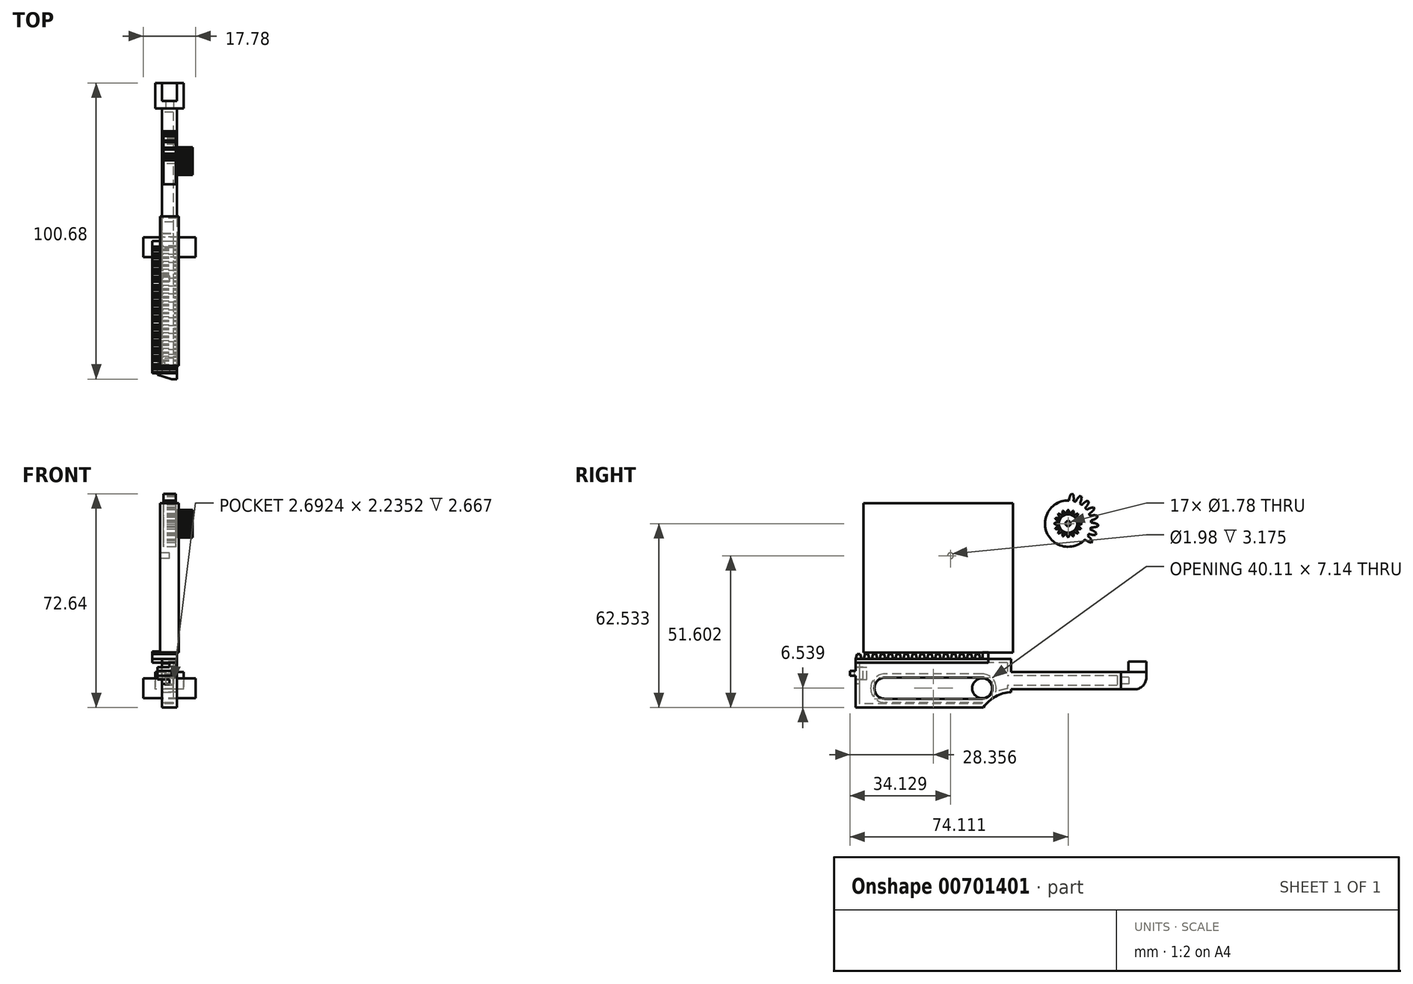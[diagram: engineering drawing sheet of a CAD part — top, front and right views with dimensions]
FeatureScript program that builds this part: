
annotation { "Feature Type Name" : "Feature", "Feature Type Description" : "" }
export const myFeature = defineFeature(function(context is Context, id is Id, definition is map)
    precondition{}
    {
        {
            var Q0;
            Q0=qCreatedBy(makeId("Right.planeOp"),FACE);
            var sketch = newSketch(context, id + "F0", { "sketchPlane" : qUnion([Q0])});
            skLineSegment(sketch, "E0.bottom", {"start": v(23, 9.46) * mm, "end": v(-29.8, 9.46) * mm});
            skLineSegment(sketch, "E0.top", {"start": v(23, -7) * mm, "end": v(-29.8, -7) * mm});
            skLineSegment(sketch, "E0.left", {"start": v(23, 9.46) * mm, "end": v(23, -7) * mm});
            skLineSegment(sketch, "E0.right", {"start": v(-29.8, 9.46) * mm, "end": v(-29.8, -7) * mm});
            skLineSegment(sketch, "E1.bottom", {"start": v(60.35, 5.06) * mm, "end": v(23, 5.06) * mm});
            skLineSegment(sketch, "E1.top", {"start": v(60.35, -0.83) * mm, "end": v(23, -0.83) * mm});
            skLineSegment(sketch, "E1.left", {"start": v(60.35, 5.06) * mm, "end": v(60.35, -0.83) * mm});
            skLineSegment(sketch, "E1.right", {"start": v(23, 5.06) * mm, "end": v(23, -0.83) * mm});
            skSolve(sketch);
        }
        {
            var Q0;
            Q0 = qSketchRegion(id + "F0", true);
            extrude(context, id + "F1", {"entities" : qUnion([Q0]), "endBound" : BoundingType.SYMMETRIC, "depth" : 5.08 * mm, "offsetDistance" : 25.4 * mm});
        }
        {
            var Q0;
            Q0=makeQuery(id+"F1.opExtrude","CAP_FACE",FACE,{"disambiguationData":[OSD([sQuery(id+"F0.wireOp",EDGE,"E0.bottom"),sQuery(id+"F0.wireOp",EDGE,"E0.top"),sQuery(id+"F0.wireOp",EDGE,"E0.left"),sQuery(id+"F0.wireOp",EDGE,"E0.right"),sQuery(id+"F0.wireOp",EDGE,"E1.bottom"),sQuery(id+"F0.wireOp",EDGE,"E1.top"),sQuery(id+"F0.wireOp",EDGE,"E1.left")])],"isStart":true});
            var sketch = newSketch(context, id + "F2", { "sketchPlane" : qUnion([Q0])});
            skLineSegment(sketch, "E2.bottom", {"start": v(-13.2, 3.1) * mm, "end": v(20, 3.1) * mm});
            skLineSegment(sketch, "E2.top", {"start": v(-13.2, -4.03) * mm, "end": v(20, -4.03) * mm});
            skLineSegment(sketch, "E2.left", {"start": v(-16.66, -0.35) * mm, "end": v(-16.66, -0.58) * mm});
            skLineSegment(sketch, "E2.right", {"start": v(23.45, -0.35) * mm, "end": v(23.45, -0.58) * mm});
            skPoint(sketch, "E3.visualSharp", {"position": v(23.45, 3.1) * mm});
            skArc(sketch, "E3.filletArc", {"start": v(23.45, -0.35) * mm, "mid": v(22.44, 2.1) * mm, "end": v(20, 3.1) * mm});
            skPoint(sketch, "E4.visualSharp", {"position": v(23.45, -4.03) * mm});
            skArc(sketch, "E4.filletArc", {"start": v(20, -4.03) * mm, "mid": v(22.44, -3.02) * mm, "end": v(23.45, -0.58) * mm});
            skPoint(sketch, "E5.visualSharp", {"position": v(-16.66, 3.1) * mm});
            skArc(sketch, "E5.filletArc", {"start": v(-13.2, 3.1) * mm, "mid": v(-15.65, 2.1) * mm, "end": v(-16.66, -0.35) * mm});
            skPoint(sketch, "E6.visualSharp", {"position": v(-16.66, -4.03) * mm});
            skArc(sketch, "E6.filletArc", {"start": v(-16.66, -0.58) * mm, "mid": v(-15.65, -3.02) * mm, "end": v(-13.2, -4.03) * mm});
            skSolve(sketch);
        }
        {
            var Q0;
            Q0 = qSketchRegion(id + "F2", true);
            var Q1;
            Q1=makeQuery(id+"F1.opExtrude","CAP_FACE",FACE,{"disambiguationData":[OSD([sQuery(id+"F0.wireOp",EDGE,"E0.bottom"),sQuery(id+"F0.wireOp",EDGE,"E0.top"),sQuery(id+"F0.wireOp",EDGE,"E0.left"),sQuery(id+"F0.wireOp",EDGE,"E0.right"),sQuery(id+"F0.wireOp",EDGE,"E1.bottom"),sQuery(id+"F0.wireOp",EDGE,"E1.top"),sQuery(id+"F0.wireOp",EDGE,"E1.left")])],"isStart":false});
            extrude(context, id + "F3", {"entities" : qUnion([Q0]), "operationType" : NewBodyOperationType.REMOVE, "endBound" : BoundingType.UP_TO_SURFACE, "oppositeDirection" : true, "depth" : 25.4 * mm, "endBoundEntityFace" : qUnion([Q1]), "offsetDistance" : 25.4 * mm});
        }
        {
            var Q0;
            Q0=makeQuery(id+"F1.opExtrude","CAP_FACE",FACE,{"disambiguationData":[OSD([sQuery(id+"F0.wireOp",EDGE,"E0.bottom"),sQuery(id+"F0.wireOp",EDGE,"E0.top"),sQuery(id+"F0.wireOp",EDGE,"E0.left"),sQuery(id+"F0.wireOp",EDGE,"E0.right"),sQuery(id+"F0.wireOp",EDGE,"E1.bottom"),sQuery(id+"F0.wireOp",EDGE,"E1.top"),sQuery(id+"F0.wireOp",EDGE,"E1.left")])],"isStart":true});
            var sketch = newSketch(context, id + "F4", { "sketchPlane" : qUnion([Q0])});
            skPoint(sketch, "E7", {"position": v(-13.61, -7) * mm});
            skPoint(sketch, "E8", {"position": v(-23, -1.8) * mm});
            skArc(sketch, "E9", {"start": v(-13.61, -7) * mm, "mid": v(-17.69, -3.27) * mm, "end": v(-23, -1.8) * mm});
            skLineSegment(sketch, "E10", {"start": v(-23, -1.8) * mm, "end": v(-23, -7) * mm});
            skLineSegment(sketch, "E11", {"start": v(-23, -7) * mm, "end": v(-13.61, -7) * mm});
            skSolve(sketch);
        }
        {
            var Q0;
            Q0=makeQuery(id+"F4.imprint","IMPRINT",FACE,{"disambiguationData":[TD([[makeQuery(id+"F4.imprint","IMPRINT",EDGE,{"derivedFrom":sQuery(id+"F4.wireOp",EDGE,"E9")}),1.0]])]});
            var Q1;
            Q1=makeQuery(id+"F1.opExtrude","CAP_FACE",FACE,{"disambiguationData":[OSD([sQuery(id+"F0.wireOp",EDGE,"E0.bottom"),sQuery(id+"F0.wireOp",EDGE,"E0.top"),sQuery(id+"F0.wireOp",EDGE,"E0.left"),sQuery(id+"F0.wireOp",EDGE,"E0.right"),sQuery(id+"F0.wireOp",EDGE,"E1.bottom"),sQuery(id+"F0.wireOp",EDGE,"E1.top"),sQuery(id+"F0.wireOp",EDGE,"E1.left")])],"isStart":false});
            extrude(context, id + "F5", {"entities" : qUnion([Q0]), "operationType" : NewBodyOperationType.REMOVE, "endBound" : BoundingType.UP_TO_SURFACE, "oppositeDirection" : true, "depth" : 25.4 * mm, "endBoundEntityFace" : qUnion([Q1]), "offsetDistance" : 25.4 * mm});
        }
        {
            var Q0;
            Q0=makeQuery(id+"F1.opExtrude","SWEPT_FACE",FACE,{"disambiguationData":[OSD([sQuery(id+"F0.wireOp",EDGE,"E1.left")])]});
            var sketch = newSketch(context, id + "F6", { "sketchPlane" : qUnion([Q0])});
            skLineSegment(sketch, "E12.bottom", {"start": v(-1.27, 3.16) * mm, "end": v(1.27, 3.16) * mm});
            skLineSegment(sketch, "E12.top", {"start": v(-1.27, 1.08) * mm, "end": v(1.27, 1.08) * mm});
            skLineSegment(sketch, "E12.left", {"start": v(-1.27, 3.16) * mm, "end": v(-1.27, 1.08) * mm});
            skLineSegment(sketch, "E12.right", {"start": v(1.27, 3.16) * mm, "end": v(1.27, 1.08) * mm});
            skSolve(sketch);
        }
        {
            var Q0;
            Q0=makeQuery(id+"F6.imprint","IMPRINT",FACE,{"disambiguationData":[TD([[makeQuery(id+"F6.imprint","IMPRINT",EDGE,{"derivedFrom":sQuery(id+"F6.wireOp",EDGE,"E12.bottom")}),-1.0]])]});
            extrude(context, id + "F7", {"entities" : qUnion([Q0]), "operationType" : NewBodyOperationType.ADD, "depth" : 2.54 * mm, "offsetDistance" : 25.4 * mm});
        }
        {
            var Q0;
            Q0=makeQuery(id+"F1.opExtrude","CAP_FACE",FACE,{"disambiguationData":[OSD([sQuery(id+"F0.wireOp",EDGE,"E0.bottom"),sQuery(id+"F0.wireOp",EDGE,"E0.top"),sQuery(id+"F0.wireOp",EDGE,"E0.left"),sQuery(id+"F0.wireOp",EDGE,"E0.right"),sQuery(id+"F0.wireOp",EDGE,"E1.bottom"),sQuery(id+"F0.wireOp",EDGE,"E1.top"),sQuery(id+"F0.wireOp",EDGE,"E1.left")])],"isStart":true});
            shell(context, id + "F8", {"entities" : qUnion([Q0]), "thickness" : 1.27 * mm});
        }
        {
            var Q0;
            Q0=makeQuery(id+"F1.opExtrude","SWEPT_FACE",FACE,{"disambiguationData":[OSD([sQuery(id+"F0.wireOp",EDGE,"E0.right")])]});
            var sketch = newSketch(context, id + "F9", { "sketchPlane" : qUnion([Q0])});
            skPoint(sketch, "E13.oppositeSnap0", {"position": v(0, 9.46) * mm});
            skLineSegment(sketch, "E13.bottom", {"start": v(-2.54, 7.93) * mm, "end": v(0, 7.93) * mm});
            skLineSegment(sketch, "E13.top", {"start": v(-2.54, 0.97) * mm, "end": v(0, 0.97) * mm});
            skLineSegment(sketch, "E13.left", {"start": v(-2.54, 7.93) * mm, "end": v(-2.54, 0.97) * mm});
            skLineSegment(sketch, "E13.right", {"start": v(0, 7.93) * mm, "end": v(0, 0.97) * mm});
            skSolve(sketch);
        }
        {
            var Q0;
            Q0=makeQuery(id+"F9.imprint","IMPRINT",FACE,{"disambiguationData":[TD([[makeQuery(id+"F9.imprint","IMPRINT",EDGE,{"derivedFrom":sQuery(id+"F9.wireOp",EDGE,"E13.bottom")}),-1.0]])]});
            var Q1;
            Q1=makeQuery(id+"F8.opShell","OFFSET_FACE",FACE,{"disambiguationData":[OSD([sQuery(id+"F0.wireOp",EDGE,"E0.right")])]});
            extrude(context, id + "F10", {"entities" : qUnion([Q0]), "operationType" : NewBodyOperationType.REMOVE, "endBound" : BoundingType.UP_TO_SURFACE, "oppositeDirection" : true, "depth" : 25.4 * mm, "endBoundEntityFace" : qUnion([Q1]), "offsetDistance" : 25.4 * mm});
        }
        {
            var Q0;
            Q0=makeQuery(id+"F10.boolean.opBoolean","COPY",FACE,{"derivedFrom":makeQuery(id+"F10.opExtrude","SWEPT_FACE",FACE,{"disambiguationData":[OSD([sQuery(id+"F9.wireOp",EDGE,"E13.right")])]})});
            var sketch = newSketch(context, id + "F11", { "sketchPlane" : qUnion([Q0])});
            skLineSegment(sketch, "E14.bottom", {"start": v(28.53, 6.66) * mm, "end": v(29.8, 6.66) * mm});
            skLineSegment(sketch, "E14.top", {"start": v(28.53, 2.5) * mm, "end": v(29.8, 2.5) * mm});
            skLineSegment(sketch, "E14.left", {"start": v(28.53, 6.66) * mm, "end": v(28.53, 2.5) * mm});
            skLineSegment(sketch, "E14.right", {"start": v(29.8, 6.66) * mm, "end": v(29.8, 2.5) * mm});
            skSolve(sketch);
        }
        {
            var Q0;
            Q0=makeQuery(id+"F11.imprint","IMPRINT",FACE,{"disambiguationData":[TD([[makeQuery(id+"F11.imprint","IMPRINT",EDGE,{"derivedFrom":sQuery(id+"F11.wireOp",EDGE,"E14.bottom")}),-1.0]])]});
            var Q1;
            Q1=makeQuery(id+"F1.opExtrude","CAP_FACE",FACE,{"disambiguationData":[OSD([sQuery(id+"F0.wireOp",EDGE,"E0.bottom"),sQuery(id+"F0.wireOp",EDGE,"E0.top"),sQuery(id+"F0.wireOp",EDGE,"E0.left"),sQuery(id+"F0.wireOp",EDGE,"E0.right"),sQuery(id+"F0.wireOp",EDGE,"E1.bottom"),sQuery(id+"F0.wireOp",EDGE,"E1.top"),sQuery(id+"F0.wireOp",EDGE,"E1.left")])],"isStart":true});
            extrude(context, id + "F12", {"entities" : qUnion([Q0]), "operationType" : NewBodyOperationType.ADD, "endBound" : BoundingType.UP_TO_SURFACE, "depth" : 25.4 * mm, "endBoundEntityFace" : qUnion([Q1]), "hasOffset" : true, "offsetDistance" : -1.52 * mm});
        }
        {
            var Q0;
            Q0=makeQuery(id+"F12.boolean.opBoolean","MERGE",FACE,{"derivedFrom":[makeQuery(id+"F8.opShell","OFFSET_FACE",FACE,{"disambiguationData":[OSD([sQuery(id+"F0.wireOp",EDGE,"E0.right")])]}),makeQuery(id+"F12.opExtrude","SWEPT_FACE",FACE,{"disambiguationData":[OSD([sQuery(id+"F11.wireOp",EDGE,"E14.left")])]})]});
            var sketch = newSketch(context, id + "F13", { "sketchPlane" : qUnion([Q0])});
            skLineSegment(sketch, "E15.bottom", {"start": v(4.06, 6.66) * mm, "end": v(2.8, 6.66) * mm});
            skLineSegment(sketch, "E15.top", {"start": v(4.06, 2.5) * mm, "end": v(2.8, 2.5) * mm});
            skLineSegment(sketch, "E15.left", {"start": v(4.06, 6.66) * mm, "end": v(4.06, 2.5) * mm});
            skLineSegment(sketch, "E15.right", {"start": v(2.8, 6.66) * mm, "end": v(2.8, 2.5) * mm});
            skSolve(sketch);
        }
        {
            var Q0;
            Q0=makeQuery(id+"F13.imprint","IMPRINT",FACE,{"disambiguationData":[TD([[makeQuery(id+"F13.imprint","IMPRINT",EDGE,{"derivedFrom":sQuery(id+"F13.wireOp",EDGE,"E15.bottom")}),1.0]])]});
            extrude(context, id + "F14", {"entities" : qUnion([Q0]), "operationType" : NewBodyOperationType.ADD, "depth" : 2.54 * mm, "offsetDistance" : 25.4 * mm});
        }
        {
            var Q0;
            Q0=makeQuery(id+"F14.boolean.opBoolean","MERGE",FACE,{"derivedFrom":[makeQuery(id+"F12.opExtrude","CAP_FACE",FACE,{"disambiguationData":[OSD([sQuery(id+"F0.wireOp",EDGE,"E0.bottom"),sQuery(id+"F0.wireOp",EDGE,"E0.top"),sQuery(id+"F0.wireOp",EDGE,"E0.left"),sQuery(id+"F0.wireOp",EDGE,"E0.right"),sQuery(id+"F0.wireOp",EDGE,"E1.bottom"),sQuery(id+"F0.wireOp",EDGE,"E1.top"),sQuery(id+"F0.wireOp",EDGE,"E1.left")])],"isStart":false}),makeQuery(id+"F14.opExtrude","SWEPT_FACE",FACE,{"disambiguationData":[OSD([sQuery(id+"F13.wireOp",EDGE,"E15.left")])]})]});
            var sketch = newSketch(context, id + "F15", { "sketchPlane" : qUnion([Q0])});
            skLineSegment(sketch, "E16.bottom", {"start": v(25.99, 2.5) * mm, "end": v(27.26, 2.5) * mm});
            skLineSegment(sketch, "E16.top", {"start": v(25.99, 6.66) * mm, "end": v(27.26, 6.66) * mm});
            skLineSegment(sketch, "E16.left", {"start": v(25.99, 2.5) * mm, "end": v(25.99, 6.66) * mm});
            skLineSegment(sketch, "E16.right", {"start": v(27.26, 2.5) * mm, "end": v(27.26, 6.66) * mm});
            skSolve(sketch);
        }
        {
            var Q0;
            Q0=makeQuery(id+"F15.imprint","IMPRINT",FACE,{"disambiguationData":[TD([[makeQuery(id+"F15.imprint","IMPRINT",EDGE,{"derivedFrom":sQuery(id+"F15.wireOp",EDGE,"E16.bottom")}),-1.0]])]});
            extrude(context, id + "F16", {"entities" : qUnion([Q0]), "operationType" : NewBodyOperationType.ADD, "depth" : -2.54 * mm, "offsetDistance" : 25.4 * mm});
        }
        {
            var Q0;
            Q0=makeQuery(id+"F12.boolean.opBoolean","MERGE",FACE,{"derivedFrom":[makeQuery(id+"F1.opExtrude","SWEPT_FACE",FACE,{"disambiguationData":[OSD([sQuery(id+"F0.wireOp",EDGE,"E0.right")])]}),makeQuery(id+"F12.opExtrude","SWEPT_FACE",FACE,{"disambiguationData":[OSD([sQuery(id+"F11.wireOp",EDGE,"E14.right")])]})]});
            var sketch = newSketch(context, id + "F17", { "sketchPlane" : qUnion([Q0])});
            skLineSegment(sketch, "E17.bottom", {"start": v(-4.06, 3.77) * mm, "end": v(2.54, 3.77) * mm});
            skLineSegment(sketch, "E17.top", {"start": v(-4.06, 5.4) * mm, "end": v(2.54, 5.4) * mm});
            skLineSegment(sketch, "E17.left", {"start": v(-4.06, 3.77) * mm, "end": v(-4.06, 5.4) * mm});
            skLineSegment(sketch, "E17.right", {"start": v(2.54, 3.77) * mm, "end": v(2.54, 5.4) * mm});
            skSolve(sketch);
        }
        {
            var Q0;
            Q0=makeQuery(id+"F17.imprint","IMPRINT",FACE,{"disambiguationData":[TD([[makeQuery(id+"F17.imprint","IMPRINT",EDGE,{"derivedFrom":sQuery(id+"F17.wireOp",EDGE,"E17.bottom")}),1.0]])]});
            extrude(context, id + "F18", {"entities" : qUnion([Q0]), "operationType" : NewBodyOperationType.ADD, "depth" : 1.96 * mm, "offsetDistance" : 25.4 * mm});
        }
        {
            var Q0;
            Q0=makeQuery(id+"F18.opExtrude","CAP_EDGE",EDGE,{"disambiguationData":[OSD([sQuery(id+"F17.wireOp",EDGE,"E17.left")])],"isStart":false});
            chamfer(context, id + "F19", {"entities" : qUnion([Q0]), "chamferType" : ChamferType.TWO_OFFSETS, "width1" : 1.52 * mm, "oppositeDirection" : false, "width2" : 4.83 * mm, "tangentPropagation" : true});
        }
        {
            var Q0;
            Q0=qCreatedBy(makeId("Right.planeOp"),FACE);
            var sketch = newSketch(context, id + "F20", { "sketchPlane" : qUnion([Q0])});
            skLineSegment(sketch, "E18.bottom", {"start": v(68.93, 8.62) * mm, "end": v(60.35, 8.62) * mm});
            skLineSegment(sketch, "E18.top", {"start": v(68.93, -0.83) * mm, "end": v(60.35, -0.83) * mm});
            skLineSegment(sketch, "E18.left", {"start": v(68.93, 8.62) * mm, "end": v(68.93, -0.83) * mm});
            skLineSegment(sketch, "E18.right", {"start": v(60.35, 8.62) * mm, "end": v(60.35, -0.83) * mm});
            skSolve(sketch);
        }
        {
            var Q0;
            Q0=makeQuery(id+"F20.imprint","IMPRINT",FACE,{"disambiguationData":[TD([[makeQuery(id+"F20.imprint","IMPRINT",EDGE,{"derivedFrom":sQuery(id+"F20.wireOp",EDGE,"E18.bottom")}),1.0]])]});
            extrude(context, id + "F21", {"entities" : qUnion([Q0]), "endBound" : BoundingType.SYMMETRIC, "depth" : 9.65 * mm, "offsetDistance" : 25.4 * mm});
        }
        {
            var Q0;
            Q0=makeQuery(id+"F21.opExtrude","SWEPT_FACE",FACE,{"disambiguationData":[OSD([sQuery(id+"F20.wireOp",EDGE,"E18.right")])]});
            var sketch = newSketch(context, id + "F22", { "sketchPlane" : qUnion([Q0])});
            skLineSegment(sketch, "E19.bottom", {"start": v(-1.35, 3.23) * mm, "end": v(1.35, 3.23) * mm});
            skLineSegment(sketch, "E19.top", {"start": v(-1.35, 1) * mm, "end": v(1.35, 1) * mm});
            skLineSegment(sketch, "E19.left", {"start": v(-1.35, 3.23) * mm, "end": v(-1.35, 1) * mm});
            skLineSegment(sketch, "E19.right", {"start": v(1.35, 3.23) * mm, "end": v(1.35, 1) * mm});
            skSolve(sketch);
        }
        {
            var Q0;
            Q0 = qSketchRegion(id + "F22", true);
            extrude(context, id + "F23", {"entities" : qUnion([Q0]), "operationType" : NewBodyOperationType.REMOVE, "oppositeDirection" : true, "depth" : 2.67 * mm, "offsetDistance" : 25.4 * mm});
        }
        {
            var Q0;
            Q0=makeQuery(id+"F21.opExtrude","SWEPT_EDGE",EDGE,{"disambiguationData":[OSD([sQuery(id+"F20.wireOp",EDGE,"E18.top"),sQuery(id+"F20.wireOp",EDGE,"E18.left")])]});
            fillet(context, id + "F24", {"entities" : qUnion([Q0]), "radius" : 4 * mm, "allowEdgeOverflow" : false});
        }
        {
            var Q0;
            Q0=makeQuery(id+"F21.opExtrude","SWEPT_FACE",FACE,{"disambiguationData":[OSD([sQuery(id+"F20.wireOp",EDGE,"E18.right")])]});
            var sketch = newSketch(context, id + "F25", { "sketchPlane" : qUnion([Q0])});
            skLineSegment(sketch, "E20.bottom", {"start": v(-4.83, 8.62) * mm, "end": v(4.83, 8.62) * mm});
            skLineSegment(sketch, "E20.top", {"start": v(-4.83, 5.06) * mm, "end": v(4.83, 5.06) * mm});
            skLineSegment(sketch, "E20.left", {"start": v(-4.83, 8.62) * mm, "end": v(-4.83, 5.06) * mm});
            skLineSegment(sketch, "E20.right", {"start": v(4.83, 8.62) * mm, "end": v(4.83, 5.06) * mm});
            skSolve(sketch);
        }
        {
            var Q0;
            Q0=makeQuery(id+"F25.imprint","IMPRINT",FACE,{"disambiguationData":[TD([[makeQuery(id+"F25.imprint","IMPRINT",EDGE,{"derivedFrom":sQuery(id+"F25.wireOp",EDGE,"E20.bottom")}),1.0]])]});
            extrude(context, id + "F26", {"entities" : qUnion([Q0]), "operationType" : NewBodyOperationType.REMOVE, "oppositeDirection" : true, "depth" : 2.54 * mm, "offsetDistance" : 25.4 * mm});
        }
        {
            var Q0;
            Q0=makeQuery(id+"F21.opExtrude","SWEPT_FACE",FACE,{"disambiguationData":[OSD([sQuery(id+"F20.wireOp",EDGE,"E18.right")])]});
            var sketch = newSketch(context, id + "F27", { "sketchPlane" : qUnion([Q0])});
            skLineSegment(sketch, "E21.bottom", {"start": v(-4.83, 5.06) * mm, "end": v(-2.54, 5.06) * mm});
            skLineSegment(sketch, "E21.top", {"start": v(-4.83, 8.62) * mm, "end": v(-2.54, 8.62) * mm});
            skLineSegment(sketch, "E21.left", {"start": v(-4.83, 5.06) * mm, "end": v(-4.83, 8.62) * mm});
            skLineSegment(sketch, "E21.right", {"start": v(-2.54, 5.06) * mm, "end": v(-2.54, 8.62) * mm});
            skLineSegment(sketch, "E22.bottom", {"start": v(2.54, 5.06) * mm, "end": v(4.83, 5.06) * mm});
            skLineSegment(sketch, "E22.top", {"start": v(2.54, 8.62) * mm, "end": v(4.83, 8.62) * mm});
            skLineSegment(sketch, "E22.left", {"start": v(2.54, 5.06) * mm, "end": v(2.54, 8.62) * mm});
            skLineSegment(sketch, "E22.right", {"start": v(4.83, 5.06) * mm, "end": v(4.83, 8.62) * mm});
            skSolve(sketch);
        }
        {
            var Q0;
            Q0=makeQuery(id+"F27.imprint","IMPRINT",FACE,{"disambiguationData":[TD([[makeQuery(id+"F27.imprint","IMPRINT",EDGE,{"derivedFrom":sQuery(id+"F27.wireOp",EDGE,"E21.bottom")}),1.0]])]});
            var Q1;
            Q1=makeQuery(id+"F27.imprint","IMPRINT",FACE,{"disambiguationData":[TD([[makeQuery(id+"F27.imprint","IMPRINT",EDGE,{"derivedFrom":sQuery(id+"F27.wireOp",EDGE,"E22.bottom")}),1.0]])]});
            var Q2;
            Q2=makeQuery(id+"F21.opExtrude","SWEPT_FACE",FACE,{"disambiguationData":[OSD([sQuery(id+"F20.wireOp",EDGE,"E18.left")])]});
            extrude(context, id + "F28", {"entities" : qUnion([Q0, Q1]), "operationType" : NewBodyOperationType.REMOVE, "endBound" : BoundingType.UP_TO_SURFACE, "oppositeDirection" : true, "depth" : 25.4 * mm, "endBoundEntityFace" : qUnion([Q2]), "offsetDistance" : 25.4 * mm});
        }
        {
            var Q0;
            Q0=qCreatedBy(makeId("Right.planeOp"),FACE);
            var sketch = newSketch(context, id + "F29", { "sketchPlane" : qUnion([Q0])});
            skCircle(sketch, "E23", {"center": v(42.36, 55.53) * mm, "radius": 7.87 * mm});
            skCircle(sketch, "E24", {"center": v(42.36, 55.53) * mm, "radius": 9.38 * mm, "construction": true});
            skCircle(sketch, "E25", {"center": v(42.36, 55.53) * mm, "radius": 10.16 * mm, "construction": true});
            skLineSegment(sketch, "E26", {"start": v(42.36, 55.53) * mm, "end": v(43.25, 68.2) * mm, "construction": true});
            skLineSegment(sketch, "E27", {"start": v(42.36, 55.53) * mm, "end": v(44.1, 68.3) * mm, "construction": true});
            skLineSegment(sketch, "E28", {"start": v(43.63, 64.82) * mm, "end": v(51.25, 64.82) * mm, "construction": true});
            skLineSegment(sketch, "E29", {"start": v(43.63, 64.82) * mm, "end": v(50.73, 62.05) * mm, "construction": true});
            skCircle(sketch, "E30", {"center": v(42.36, 55.53) * mm, "radius": 9.11 * mm, "construction": true});
            skCircle(sketch, "E31", {"center": v(43.02, 64.89) * mm, "radius": 5.08 * mm, "construction": true});
            skCircle(sketch, "E32", {"center": v(47.7, 62.91) * mm, "radius": 5.08 * mm, "construction": true});
            skArc(sketch, "E33", {"start": v(43.41, 65.64) * mm, "mid": v(43.14, 65.15) * mm, "end": v(42.92, 64.63) * mm});
            skArc(sketch, "E34", {"start": v(42.92, 64.63) * mm, "mid": v(42.75, 64.02) * mm, "end": v(42.65, 63.4) * mm});
            skArc(sketch, "E35.MirrorCS", {"start": v(44.06, 65.55) * mm, "mid": v(44.2, 65) * mm, "end": v(44.26, 64.44) * mm});
            skArc(sketch, "E36.MirrorCS", {"start": v(44.26, 64.44) * mm, "mid": v(44.27, 63.81) * mm, "end": v(44.2, 63.19) * mm});
            skLineSegment(sketch, "E37", {"start": v(44.06, 65.55) * mm, "end": v(43.41, 65.64) * mm});
            skSolve(sketch);
        }
        {
            var Q0;
            Q0=makeQuery(id+"F29.imprint","IMPRINT",FACE,{"disambiguationData":[TD([[makeQuery(id+"F29.imprint","IMPRINT",EDGE,{"derivedFrom":sQuery(id+"F29.wireOp",EDGE,"E33")}),1.0]])]});
            var Q1;
            {var subQ0=sQuery(id+"F29.wireOp",EDGE,"E23");var subQ1=makeQuery(id+"F29.imprint","INTERSECT",VERTEX,{"derivedFrom":[subQ0,sQuery(id+"F29.wireOp",EDGE,"E34")]});Q1=makeQuery(id+"F29.imprint","IMPRINT",FACE,{"disambiguationData":[TD([[makeQuery(id+"F29.imprint","IMPRINT",EDGE,{"disambiguationData":[TD([[subQ1,1.0]])],"derivedFrom":subQ0}),1.0]])]});}
            extrude(context, id + "F30", {"entities" : qUnion([Q0, Q1]), "endBound" : BoundingType.SYMMETRIC, "depth" : 4.1 * mm, "offsetDistance" : 25.4 * mm});
        }
        {
            var Q0;
            Q0=makeQuery(id+"F30.opExtrude","SWEPT_BODY",BODY,{"disambiguationData":[OSD([sQuery(id+"F29.wireOp",EDGE,"E23"),sQuery(id+"F29.wireOp",EDGE,"UvCLlL38-NRi8-EqfE-xOJT-4VXvg5Cvypkm"),sQuery(id+"F29.wireOp",EDGE,"AdAfBMBF-3M5v-ihU7-Tuhu-rgdGBiSxAzMV"),sQuery(id+"F29.wireOp",EDGE,"44965daa-e4ee-4ec7-b42b-ffab7727ce9d0.MirrorCS"),sQuery(id+"F29.wireOp",EDGE,"9c7dd22d-d60f-46b9-b6e2-b66cb8bc2ee40.MirrorCS"),sQuery(id+"F29.wireOp",EDGE,"fpTgo57x-aQlM-V4Xv-RvaO-GCsvssqiRATg")])]});
            var Q1;
            Q1=makeQuery(id+"F30.opExtrude","SWEPT_FACE",FACE,{"disambiguationData":[OSD([sQuery(id+"F29.wireOp",EDGE,"E23")])]});
            circularPattern(context, id + "F31", {"entities" : qUnion([Q0]), "axis" : qUnion([Q1]), "angle" : 120 * degree, "instanceCount" : 8, "equalSpace" : true});
        }
        {
            var Q0;
            Q0=makeQuery(id+"F30.opExtrude","SWEPT_BODY",BODY,{"disambiguationData":[OSD([sQuery(id+"F29.wireOp",EDGE,"E23"),sQuery(id+"F29.wireOp",EDGE,"UvCLlL38-NRi8-EqfE-xOJT-4VXvg5Cvypkm"),sQuery(id+"F29.wireOp",EDGE,"AdAfBMBF-3M5v-ihU7-Tuhu-rgdGBiSxAzMV"),sQuery(id+"F29.wireOp",EDGE,"44965daa-e4ee-4ec7-b42b-ffab7727ce9d0.MirrorCS"),sQuery(id+"F29.wireOp",EDGE,"9c7dd22d-d60f-46b9-b6e2-b66cb8bc2ee40.MirrorCS"),sQuery(id+"F29.wireOp",EDGE,"fpTgo57x-aQlM-V4Xv-RvaO-GCsvssqiRATg")])]});
            var Q1;
            Q1=makeQuery(id+"F31.opPattern","COPY",BODY,{"derivedFrom":makeQuery(id+"F30.opExtrude","SWEPT_BODY",BODY,{"disambiguationData":[OSD([sQuery(id+"F29.wireOp",EDGE,"E23"),sQuery(id+"F29.wireOp",EDGE,"UvCLlL38-NRi8-EqfE-xOJT-4VXvg5Cvypkm"),sQuery(id+"F29.wireOp",EDGE,"AdAfBMBF-3M5v-ihU7-Tuhu-rgdGBiSxAzMV"),sQuery(id+"F29.wireOp",EDGE,"44965daa-e4ee-4ec7-b42b-ffab7727ce9d0.MirrorCS"),sQuery(id+"F29.wireOp",EDGE,"9c7dd22d-d60f-46b9-b6e2-b66cb8bc2ee40.MirrorCS"),sQuery(id+"F29.wireOp",EDGE,"fpTgo57x-aQlM-V4Xv-RvaO-GCsvssqiRATg")])]}),"instanceName":"1"});
            var Q2;
            Q2=makeQuery(id+"F31.opPattern","COPY",BODY,{"derivedFrom":makeQuery(id+"F30.opExtrude","SWEPT_BODY",BODY,{"disambiguationData":[OSD([sQuery(id+"F29.wireOp",EDGE,"E23"),sQuery(id+"F29.wireOp",EDGE,"UvCLlL38-NRi8-EqfE-xOJT-4VXvg5Cvypkm"),sQuery(id+"F29.wireOp",EDGE,"AdAfBMBF-3M5v-ihU7-Tuhu-rgdGBiSxAzMV"),sQuery(id+"F29.wireOp",EDGE,"44965daa-e4ee-4ec7-b42b-ffab7727ce9d0.MirrorCS"),sQuery(id+"F29.wireOp",EDGE,"9c7dd22d-d60f-46b9-b6e2-b66cb8bc2ee40.MirrorCS"),sQuery(id+"F29.wireOp",EDGE,"fpTgo57x-aQlM-V4Xv-RvaO-GCsvssqiRATg")])]}),"instanceName":"2"});
            var Q3;
            Q3=makeQuery(id+"F31.opPattern","COPY",BODY,{"derivedFrom":makeQuery(id+"F30.opExtrude","SWEPT_BODY",BODY,{"disambiguationData":[OSD([sQuery(id+"F29.wireOp",EDGE,"E23"),sQuery(id+"F29.wireOp",EDGE,"UvCLlL38-NRi8-EqfE-xOJT-4VXvg5Cvypkm"),sQuery(id+"F29.wireOp",EDGE,"AdAfBMBF-3M5v-ihU7-Tuhu-rgdGBiSxAzMV"),sQuery(id+"F29.wireOp",EDGE,"44965daa-e4ee-4ec7-b42b-ffab7727ce9d0.MirrorCS"),sQuery(id+"F29.wireOp",EDGE,"9c7dd22d-d60f-46b9-b6e2-b66cb8bc2ee40.MirrorCS"),sQuery(id+"F29.wireOp",EDGE,"fpTgo57x-aQlM-V4Xv-RvaO-GCsvssqiRATg")])]}),"instanceName":"3"});
            var Q4;
            Q4=makeQuery(id+"F31.opPattern","COPY",BODY,{"derivedFrom":makeQuery(id+"F30.opExtrude","SWEPT_BODY",BODY,{"disambiguationData":[OSD([sQuery(id+"F29.wireOp",EDGE,"E23"),sQuery(id+"F29.wireOp",EDGE,"UvCLlL38-NRi8-EqfE-xOJT-4VXvg5Cvypkm"),sQuery(id+"F29.wireOp",EDGE,"AdAfBMBF-3M5v-ihU7-Tuhu-rgdGBiSxAzMV"),sQuery(id+"F29.wireOp",EDGE,"44965daa-e4ee-4ec7-b42b-ffab7727ce9d0.MirrorCS"),sQuery(id+"F29.wireOp",EDGE,"9c7dd22d-d60f-46b9-b6e2-b66cb8bc2ee40.MirrorCS"),sQuery(id+"F29.wireOp",EDGE,"fpTgo57x-aQlM-V4Xv-RvaO-GCsvssqiRATg")])]}),"instanceName":"4"});
            var Q5;
            Q5=makeQuery(id+"F31.opPattern","COPY",BODY,{"derivedFrom":makeQuery(id+"F30.opExtrude","SWEPT_BODY",BODY,{"disambiguationData":[OSD([sQuery(id+"F29.wireOp",EDGE,"E23"),sQuery(id+"F29.wireOp",EDGE,"UvCLlL38-NRi8-EqfE-xOJT-4VXvg5Cvypkm"),sQuery(id+"F29.wireOp",EDGE,"AdAfBMBF-3M5v-ihU7-Tuhu-rgdGBiSxAzMV"),sQuery(id+"F29.wireOp",EDGE,"44965daa-e4ee-4ec7-b42b-ffab7727ce9d0.MirrorCS"),sQuery(id+"F29.wireOp",EDGE,"9c7dd22d-d60f-46b9-b6e2-b66cb8bc2ee40.MirrorCS"),sQuery(id+"F29.wireOp",EDGE,"fpTgo57x-aQlM-V4Xv-RvaO-GCsvssqiRATg")])]}),"instanceName":"5"});
            var Q6;
            Q6=makeQuery(id+"F31.opPattern","COPY",BODY,{"derivedFrom":makeQuery(id+"F30.opExtrude","SWEPT_BODY",BODY,{"disambiguationData":[OSD([sQuery(id+"F29.wireOp",EDGE,"E23"),sQuery(id+"F29.wireOp",EDGE,"UvCLlL38-NRi8-EqfE-xOJT-4VXvg5Cvypkm"),sQuery(id+"F29.wireOp",EDGE,"AdAfBMBF-3M5v-ihU7-Tuhu-rgdGBiSxAzMV"),sQuery(id+"F29.wireOp",EDGE,"44965daa-e4ee-4ec7-b42b-ffab7727ce9d0.MirrorCS"),sQuery(id+"F29.wireOp",EDGE,"9c7dd22d-d60f-46b9-b6e2-b66cb8bc2ee40.MirrorCS"),sQuery(id+"F29.wireOp",EDGE,"fpTgo57x-aQlM-V4Xv-RvaO-GCsvssqiRATg")])]}),"instanceName":"6"});
            var Q7;
            Q7=makeQuery(id+"F31.opPattern","COPY",BODY,{"derivedFrom":makeQuery(id+"F30.opExtrude","SWEPT_BODY",BODY,{"disambiguationData":[OSD([sQuery(id+"F29.wireOp",EDGE,"E23"),sQuery(id+"F29.wireOp",EDGE,"UvCLlL38-NRi8-EqfE-xOJT-4VXvg5Cvypkm"),sQuery(id+"F29.wireOp",EDGE,"AdAfBMBF-3M5v-ihU7-Tuhu-rgdGBiSxAzMV"),sQuery(id+"F29.wireOp",EDGE,"44965daa-e4ee-4ec7-b42b-ffab7727ce9d0.MirrorCS"),sQuery(id+"F29.wireOp",EDGE,"9c7dd22d-d60f-46b9-b6e2-b66cb8bc2ee40.MirrorCS"),sQuery(id+"F29.wireOp",EDGE,"fpTgo57x-aQlM-V4Xv-RvaO-GCsvssqiRATg")])]}),"instanceName":"7"});
            var Q8;
            Q8=makeQuery(id+"F31.opPattern","COPY",BODY,{"derivedFrom":makeQuery(id+"F30.opExtrude","SWEPT_BODY",BODY,{"disambiguationData":[OSD([sQuery(id+"F29.wireOp",EDGE,"E23"),sQuery(id+"F29.wireOp",EDGE,"UvCLlL38-NRi8-EqfE-xOJT-4VXvg5Cvypkm"),sQuery(id+"F29.wireOp",EDGE,"AdAfBMBF-3M5v-ihU7-Tuhu-rgdGBiSxAzMV"),sQuery(id+"F29.wireOp",EDGE,"44965daa-e4ee-4ec7-b42b-ffab7727ce9d0.MirrorCS"),sQuery(id+"F29.wireOp",EDGE,"9c7dd22d-d60f-46b9-b6e2-b66cb8bc2ee40.MirrorCS"),sQuery(id+"F29.wireOp",EDGE,"fpTgo57x-aQlM-V4Xv-RvaO-GCsvssqiRATg")])]}),"instanceName":"9"});
            var Q9;
            Q9=makeQuery(id+"F31.opPattern","COPY",BODY,{"derivedFrom":makeQuery(id+"F30.opExtrude","SWEPT_BODY",BODY,{"disambiguationData":[OSD([sQuery(id+"F29.wireOp",EDGE,"E23"),sQuery(id+"F29.wireOp",EDGE,"UvCLlL38-NRi8-EqfE-xOJT-4VXvg5Cvypkm"),sQuery(id+"F29.wireOp",EDGE,"AdAfBMBF-3M5v-ihU7-Tuhu-rgdGBiSxAzMV"),sQuery(id+"F29.wireOp",EDGE,"44965daa-e4ee-4ec7-b42b-ffab7727ce9d0.MirrorCS"),sQuery(id+"F29.wireOp",EDGE,"9c7dd22d-d60f-46b9-b6e2-b66cb8bc2ee40.MirrorCS"),sQuery(id+"F29.wireOp",EDGE,"fpTgo57x-aQlM-V4Xv-RvaO-GCsvssqiRATg")])]}),"instanceName":"10"});
            var Q10;
            Q10=makeQuery(id+"F31.opPattern","COPY",BODY,{"derivedFrom":makeQuery(id+"F30.opExtrude","SWEPT_BODY",BODY,{"disambiguationData":[OSD([sQuery(id+"F29.wireOp",EDGE,"E23"),sQuery(id+"F29.wireOp",EDGE,"UvCLlL38-NRi8-EqfE-xOJT-4VXvg5Cvypkm"),sQuery(id+"F29.wireOp",EDGE,"AdAfBMBF-3M5v-ihU7-Tuhu-rgdGBiSxAzMV"),sQuery(id+"F29.wireOp",EDGE,"44965daa-e4ee-4ec7-b42b-ffab7727ce9d0.MirrorCS"),sQuery(id+"F29.wireOp",EDGE,"9c7dd22d-d60f-46b9-b6e2-b66cb8bc2ee40.MirrorCS"),sQuery(id+"F29.wireOp",EDGE,"fpTgo57x-aQlM-V4Xv-RvaO-GCsvssqiRATg")])]}),"instanceName":"11"});
            var Q11;
            Q11=makeQuery(id+"F31.opPattern","COPY",BODY,{"derivedFrom":makeQuery(id+"F30.opExtrude","SWEPT_BODY",BODY,{"disambiguationData":[OSD([sQuery(id+"F29.wireOp",EDGE,"E23"),sQuery(id+"F29.wireOp",EDGE,"UvCLlL38-NRi8-EqfE-xOJT-4VXvg5Cvypkm"),sQuery(id+"F29.wireOp",EDGE,"AdAfBMBF-3M5v-ihU7-Tuhu-rgdGBiSxAzMV"),sQuery(id+"F29.wireOp",EDGE,"44965daa-e4ee-4ec7-b42b-ffab7727ce9d0.MirrorCS"),sQuery(id+"F29.wireOp",EDGE,"9c7dd22d-d60f-46b9-b6e2-b66cb8bc2ee40.MirrorCS"),sQuery(id+"F29.wireOp",EDGE,"fpTgo57x-aQlM-V4Xv-RvaO-GCsvssqiRATg")])]}),"instanceName":"12"});
            var Q12;
            Q12=makeQuery(id+"F31.opPattern","COPY",BODY,{"derivedFrom":makeQuery(id+"F30.opExtrude","SWEPT_BODY",BODY,{"disambiguationData":[OSD([sQuery(id+"F29.wireOp",EDGE,"E23"),sQuery(id+"F29.wireOp",EDGE,"UvCLlL38-NRi8-EqfE-xOJT-4VXvg5Cvypkm"),sQuery(id+"F29.wireOp",EDGE,"AdAfBMBF-3M5v-ihU7-Tuhu-rgdGBiSxAzMV"),sQuery(id+"F29.wireOp",EDGE,"44965daa-e4ee-4ec7-b42b-ffab7727ce9d0.MirrorCS"),sQuery(id+"F29.wireOp",EDGE,"9c7dd22d-d60f-46b9-b6e2-b66cb8bc2ee40.MirrorCS"),sQuery(id+"F29.wireOp",EDGE,"fpTgo57x-aQlM-V4Xv-RvaO-GCsvssqiRATg")])]}),"instanceName":"13"});
            var Q13;
            Q13=makeQuery(id+"F31.opPattern","COPY",BODY,{"derivedFrom":makeQuery(id+"F30.opExtrude","SWEPT_BODY",BODY,{"disambiguationData":[OSD([sQuery(id+"F29.wireOp",EDGE,"E23"),sQuery(id+"F29.wireOp",EDGE,"UvCLlL38-NRi8-EqfE-xOJT-4VXvg5Cvypkm"),sQuery(id+"F29.wireOp",EDGE,"AdAfBMBF-3M5v-ihU7-Tuhu-rgdGBiSxAzMV"),sQuery(id+"F29.wireOp",EDGE,"44965daa-e4ee-4ec7-b42b-ffab7727ce9d0.MirrorCS"),sQuery(id+"F29.wireOp",EDGE,"9c7dd22d-d60f-46b9-b6e2-b66cb8bc2ee40.MirrorCS"),sQuery(id+"F29.wireOp",EDGE,"fpTgo57x-aQlM-V4Xv-RvaO-GCsvssqiRATg")])]}),"instanceName":"14"});
            var Q14;
            Q14=makeQuery(id+"F31.opPattern","COPY",BODY,{"derivedFrom":makeQuery(id+"F30.opExtrude","SWEPT_BODY",BODY,{"disambiguationData":[OSD([sQuery(id+"F29.wireOp",EDGE,"E23"),sQuery(id+"F29.wireOp",EDGE,"UvCLlL38-NRi8-EqfE-xOJT-4VXvg5Cvypkm"),sQuery(id+"F29.wireOp",EDGE,"AdAfBMBF-3M5v-ihU7-Tuhu-rgdGBiSxAzMV"),sQuery(id+"F29.wireOp",EDGE,"44965daa-e4ee-4ec7-b42b-ffab7727ce9d0.MirrorCS"),sQuery(id+"F29.wireOp",EDGE,"9c7dd22d-d60f-46b9-b6e2-b66cb8bc2ee40.MirrorCS"),sQuery(id+"F29.wireOp",EDGE,"fpTgo57x-aQlM-V4Xv-RvaO-GCsvssqiRATg")])]}),"instanceName":"15"});
            var Q15;
            Q15=makeQuery(id+"F31.opPattern","COPY",BODY,{"derivedFrom":makeQuery(id+"F30.opExtrude","SWEPT_BODY",BODY,{"disambiguationData":[OSD([sQuery(id+"F29.wireOp",EDGE,"E23"),sQuery(id+"F29.wireOp",EDGE,"UvCLlL38-NRi8-EqfE-xOJT-4VXvg5Cvypkm"),sQuery(id+"F29.wireOp",EDGE,"AdAfBMBF-3M5v-ihU7-Tuhu-rgdGBiSxAzMV"),sQuery(id+"F29.wireOp",EDGE,"44965daa-e4ee-4ec7-b42b-ffab7727ce9d0.MirrorCS"),sQuery(id+"F29.wireOp",EDGE,"9c7dd22d-d60f-46b9-b6e2-b66cb8bc2ee40.MirrorCS"),sQuery(id+"F29.wireOp",EDGE,"fpTgo57x-aQlM-V4Xv-RvaO-GCsvssqiRATg")])]}),"instanceName":"16"});
            var Q16;
            Q16=makeQuery(id+"F31.opPattern","COPY",BODY,{"derivedFrom":makeQuery(id+"F30.opExtrude","SWEPT_BODY",BODY,{"disambiguationData":[OSD([sQuery(id+"F29.wireOp",EDGE,"E23"),sQuery(id+"F29.wireOp",EDGE,"UvCLlL38-NRi8-EqfE-xOJT-4VXvg5Cvypkm"),sQuery(id+"F29.wireOp",EDGE,"AdAfBMBF-3M5v-ihU7-Tuhu-rgdGBiSxAzMV"),sQuery(id+"F29.wireOp",EDGE,"44965daa-e4ee-4ec7-b42b-ffab7727ce9d0.MirrorCS"),sQuery(id+"F29.wireOp",EDGE,"9c7dd22d-d60f-46b9-b6e2-b66cb8bc2ee40.MirrorCS"),sQuery(id+"F29.wireOp",EDGE,"fpTgo57x-aQlM-V4Xv-RvaO-GCsvssqiRATg")])]}),"instanceName":"17"});
            booleanBodies(context, id + "F32", {"operationType" : BooleanOperationType.UNION, "tools" : qUnion([Q0, Q1, Q2, Q3, Q4, Q5, Q6, Q7, Q8, Q9, Q10, Q11, Q12, Q13, Q14, Q15, Q16])});
        }
        {
            var Q0;
            Q0=qCreatedBy(makeId("Right.planeOp"),FACE);
            var sketch = newSketch(context, id + "F33", { "sketchPlane" : qUnion([Q0])});
            skCircle(sketch, "E38", {"center": v(13.16, -0.48) * mm, "radius": 3.4 * mm});
            skSolve(sketch);
        }
        {
            var Q0;
            Q0 = qSketchRegion(id + "F33", true);
            extrude(context, id + "F34", {"entities" : qUnion([Q0]), "endBound" : BoundingType.SYMMETRIC, "depth" : 17.78 * mm, "offsetDistance" : 25.4 * mm});
        }
        {
            var Q0;
            {var subQ0=makeQuery(id+"F30.opExtrude","CAP_FACE",FACE,{"disambiguationData":[OSD([sQuery(id+"F29.wireOp",EDGE,"E23"),sQuery(id+"F29.wireOp",EDGE,"E33"),sQuery(id+"F29.wireOp",EDGE,"E34"),sQuery(id+"F29.wireOp",EDGE,"E35.MirrorCS"),sQuery(id+"F29.wireOp",EDGE,"E36.MirrorCS"),sQuery(id+"F29.wireOp",EDGE,"E37")])],"isStart":true});Q0=makeQuery(id+"F32.opBoolean","MERGE",FACE,{"derivedFrom":[subQ0,makeQuery(id+"F31.opPattern","COPY",FACE,{"derivedFrom":subQ0,"instanceName":"1"}),makeQuery(id+"F31.opPattern","COPY",FACE,{"derivedFrom":subQ0,"instanceName":"2"}),makeQuery(id+"F31.opPattern","COPY",FACE,{"derivedFrom":subQ0,"instanceName":"3"}),makeQuery(id+"F31.opPattern","COPY",FACE,{"derivedFrom":subQ0,"instanceName":"4"}),makeQuery(id+"F31.opPattern","COPY",FACE,{"derivedFrom":subQ0,"instanceName":"5"}),makeQuery(id+"F31.opPattern","COPY",FACE,{"derivedFrom":subQ0,"instanceName":"6"}),makeQuery(id+"F31.opPattern","COPY",FACE,{"derivedFrom":subQ0,"instanceName":"7"})]});}
            var sketch = newSketch(context, id + "F35", { "sketchPlane" : qUnion([Q0])});
            skCircle(sketch, "E39", {"center": v(-42.36, 55.53) * mm, "radius": 0.89 * mm});
            skSolve(sketch);
        }
        {
            var Q0;
            Q0=makeQuery(id+"F35.imprint","IMPRINT",FACE,{"disambiguationData":[TD([[makeQuery(id+"F35.imprint","IMPRINT",EDGE,{"derivedFrom":sQuery(id+"F35.wireOp",EDGE,"E39")}),1.0]])]});
            var Q1;
            {var subQ0=makeQuery(id+"F30.opExtrude","CAP_FACE",FACE,{"disambiguationData":[OSD([sQuery(id+"F29.wireOp",EDGE,"E23"),sQuery(id+"F29.wireOp",EDGE,"E33"),sQuery(id+"F29.wireOp",EDGE,"E34"),sQuery(id+"F29.wireOp",EDGE,"E35.MirrorCS"),sQuery(id+"F29.wireOp",EDGE,"E36.MirrorCS"),sQuery(id+"F29.wireOp",EDGE,"E37")])],"isStart":false});Q1=makeQuery(id+"F32.opBoolean","MERGE",FACE,{"derivedFrom":[subQ0,makeQuery(id+"F31.opPattern","COPY",FACE,{"derivedFrom":subQ0,"instanceName":"1"}),makeQuery(id+"F31.opPattern","COPY",FACE,{"derivedFrom":subQ0,"instanceName":"2"}),makeQuery(id+"F31.opPattern","COPY",FACE,{"derivedFrom":subQ0,"instanceName":"3"}),makeQuery(id+"F31.opPattern","COPY",FACE,{"derivedFrom":subQ0,"instanceName":"4"}),makeQuery(id+"F31.opPattern","COPY",FACE,{"derivedFrom":subQ0,"instanceName":"5"}),makeQuery(id+"F31.opPattern","COPY",FACE,{"derivedFrom":subQ0,"instanceName":"6"}),makeQuery(id+"F31.opPattern","COPY",FACE,{"derivedFrom":subQ0,"instanceName":"7"})]});}
            extrude(context, id + "F36", {"entities" : qUnion([Q0]), "operationType" : NewBodyOperationType.REMOVE, "endBound" : BoundingType.UP_TO_SURFACE, "oppositeDirection" : true, "depth" : 25.4 * mm, "endBoundEntityFace" : qUnion([Q1]), "offsetDistance" : 25.4 * mm});
        }
        {
            var Q0;
            Q0=qCreatedBy(makeId("Right.planeOp"),FACE);
            var sketch = newSketch(context, id + "F37", { "sketchPlane" : qUnion([Q0])});
            skLineSegment(sketch, "E40.bottom", {"start": v(23.62, 62.42) * mm, "end": v(-27.18, 62.42) * mm});
            skLineSegment(sketch, "E40.top", {"start": v(23.62, 11.62) * mm, "end": v(-27.18, 11.62) * mm});
            skLineSegment(sketch, "E40.left", {"start": v(23.62, 62.42) * mm, "end": v(23.62, 11.62) * mm});
            skLineSegment(sketch, "E40.right", {"start": v(-27.18, 62.42) * mm, "end": v(-27.18, 11.62) * mm});
            skCircle(sketch, "E41", {"center": v(2.38, 44.6) * mm, "radius": 1 * mm});
            skSolve(sketch);
        }
        {
            var Q0;
            Q0=makeQuery(id+"F37.imprint","IMPRINT",FACE,{"disambiguationData":[TD([[makeQuery(id+"F37.imprint","IMPRINT",EDGE,{"derivedFrom":sQuery(id+"F37.wireOp",EDGE,"E40.bottom")}),1.0]])]});
            extrude(context, id + "F38", {"entities" : qUnion([Q0]), "endBound" : BoundingType.SYMMETRIC, "depth" : 6.35 * mm, "offsetDistance" : 25.4 * mm});
        }
        {
            var Q0;
            Q0=makeQuery(id+"F37.imprint","IMPRINT",FACE,{"disambiguationData":[TD([[makeQuery(id+"F37.imprint","IMPRINT",EDGE,{"derivedFrom":sQuery(id+"F37.wireOp",EDGE,"E41")}),1.0]])]});
            var Q1;
            Q1=makeQuery(id+"F38.opExtrude","CAP_FACE",FACE,{"disambiguationData":[OSD([sQuery(id+"F37.wireOp",EDGE,"E40.bottom"),sQuery(id+"F37.wireOp",EDGE,"E40.top"),sQuery(id+"F37.wireOp",EDGE,"E40.left"),sQuery(id+"F37.wireOp",EDGE,"E40.right"),sQuery(id+"F37.wireOp",EDGE,"E41")])],"isStart":false});
            extrude(context, id + "F39", {"entities" : qUnion([Q0]), "operationType" : NewBodyOperationType.ADD, "endBound" : BoundingType.UP_TO_SURFACE, "depth" : 25.4 * mm, "endBoundEntityFace" : qUnion([Q1]), "offsetDistance" : 25.4 * mm});
        }
        {
            var Q0;
            Q0=makeQuery(id+"F18.boolean.opBoolean","MERGE",FACE,{"derivedFrom":[makeQuery(id+"F1.opExtrude","CAP_FACE",FACE,{"disambiguationData":[OSD([sQuery(id+"F0.wireOp",EDGE,"E0.bottom"),sQuery(id+"F0.wireOp",EDGE,"E0.top"),sQuery(id+"F0.wireOp",EDGE,"E0.left"),sQuery(id+"F0.wireOp",EDGE,"E0.right"),sQuery(id+"F0.wireOp",EDGE,"E1.bottom"),sQuery(id+"F0.wireOp",EDGE,"E1.top"),sQuery(id+"F0.wireOp",EDGE,"E1.left")])],"isStart":false}),makeQuery(id+"F18.opExtrude","SWEPT_FACE",FACE,{"disambiguationData":[OSD([sQuery(id+"F17.wireOp",EDGE,"E17.right")])]})]});
            var sketch = newSketch(context, id + "F40", { "sketchPlane" : qUnion([Q0])});
            skLineSegment(sketch, "E42", {"start": v(-29.32, 11.12) * mm, "end": v(-28.3, 11.12) * mm});
            skLineSegment(sketch, "E43", {"start": v(-28.3, 11.12) * mm, "end": v(-27.82, 9.45) * mm});
            skLineSegment(sketch, "E44", {"start": v(-28.8, 11.12) * mm, "end": v(-28.8, 9.17) * mm, "construction": true});
            skLineSegment(sketch, "E45.MirrorCS", {"start": v(-29.32, 11.12) * mm, "end": v(-29.8, 9.46) * mm});
            skLineSegment(sketch, "E46", {"start": v(-29.8, 9.46) * mm, "end": v(-27.82, 9.45) * mm});
            skLineSegment(sketch, "E47.top", {"start": v(8.53, 9.46) * mm, "end": v(15.24, 9.46) * mm});
            skLineSegment(sketch, "E48.1.0.0", {"start": v(-26.63, 11.12) * mm, "end": v(-27.1, 9.46) * mm});
            skLineSegment(sketch, "E48.1.0.1", {"start": v(-26.63, 11.12) * mm, "end": v(-25.6, 11.12) * mm});
            skLineSegment(sketch, "E48.1.0.2", {"start": v(-27.1, 9.46) * mm, "end": v(-25.13, 9.45) * mm});
            skLineSegment(sketch, "E48.1.0.3", {"start": v(-25.6, 11.12) * mm, "end": v(-25.13, 9.45) * mm});
            skLineSegment(sketch, "E48.2.0.0", {"start": v(-23.94, 11.12) * mm, "end": v(-24.41, 9.46) * mm});
            skLineSegment(sketch, "E48.2.0.1", {"start": v(-23.94, 11.12) * mm, "end": v(-22.9, 11.12) * mm});
            skLineSegment(sketch, "E48.2.0.2", {"start": v(-24.41, 9.46) * mm, "end": v(-22.43, 9.45) * mm});
            skLineSegment(sketch, "E48.2.0.3", {"start": v(-22.9, 11.12) * mm, "end": v(-22.43, 9.45) * mm});
            skLineSegment(sketch, "E48.3.0.0", {"start": v(-21.24, 11.12) * mm, "end": v(-21.72, 9.46) * mm});
            skLineSegment(sketch, "E48.3.0.1", {"start": v(-21.24, 11.12) * mm, "end": v(-20.21, 11.12) * mm});
            skLineSegment(sketch, "E48.3.0.2", {"start": v(-21.72, 9.46) * mm, "end": v(-19.74, 9.45) * mm});
            skLineSegment(sketch, "E48.3.0.3", {"start": v(-20.21, 11.12) * mm, "end": v(-19.74, 9.45) * mm});
            skLineSegment(sketch, "E48.4.0.0", {"start": v(-18.55, 11.12) * mm, "end": v(-19.03, 9.46) * mm});
            skLineSegment(sketch, "E48.4.0.1", {"start": v(-18.55, 11.12) * mm, "end": v(-17.52, 11.12) * mm});
            skLineSegment(sketch, "E48.4.0.2", {"start": v(-19.03, 9.46) * mm, "end": v(-17.05, 9.45) * mm});
            skLineSegment(sketch, "E48.4.0.3", {"start": v(-17.52, 11.12) * mm, "end": v(-17.05, 9.45) * mm});
            skLineSegment(sketch, "E48.5.0.0", {"start": v(-15.86, 11.12) * mm, "end": v(-16.34, 9.46) * mm});
            skLineSegment(sketch, "E48.5.0.1", {"start": v(-15.86, 11.12) * mm, "end": v(-14.83, 11.12) * mm});
            skLineSegment(sketch, "E48.5.0.2", {"start": v(-16.34, 9.46) * mm, "end": v(-14.36, 9.45) * mm});
            skLineSegment(sketch, "E48.5.0.3", {"start": v(-14.83, 11.12) * mm, "end": v(-14.36, 9.45) * mm});
            skLineSegment(sketch, "E48.6.0.0", {"start": v(-13.17, 11.12) * mm, "end": v(-13.64, 9.46) * mm});
            skLineSegment(sketch, "E48.6.0.1", {"start": v(-13.17, 11.12) * mm, "end": v(-12.14, 11.12) * mm});
            skLineSegment(sketch, "E48.6.0.2", {"start": v(-13.64, 9.46) * mm, "end": v(-11.66, 9.45) * mm});
            skLineSegment(sketch, "E48.6.0.3", {"start": v(-12.14, 11.12) * mm, "end": v(-11.66, 9.45) * mm});
            skLineSegment(sketch, "E48.7.0.0", {"start": v(-10.47, 11.12) * mm, "end": v(-10.95, 9.46) * mm});
            skLineSegment(sketch, "E48.7.0.1", {"start": v(-10.47, 11.12) * mm, "end": v(-9.44, 11.12) * mm});
            skLineSegment(sketch, "E48.7.0.2", {"start": v(-10.95, 9.46) * mm, "end": v(-8.97, 9.45) * mm});
            skLineSegment(sketch, "E48.7.0.3", {"start": v(-9.44, 11.12) * mm, "end": v(-8.97, 9.45) * mm});
            skLineSegment(sketch, "E48.8.0.0", {"start": v(-7.78, 11.12) * mm, "end": v(-8.26, 9.46) * mm});
            skLineSegment(sketch, "E48.8.0.1", {"start": v(-7.78, 11.12) * mm, "end": v(-6.75, 11.12) * mm});
            skLineSegment(sketch, "E48.8.0.2", {"start": v(-8.26, 9.46) * mm, "end": v(-6.28, 9.45) * mm});
            skLineSegment(sketch, "E48.8.0.3", {"start": v(-6.75, 11.12) * mm, "end": v(-6.28, 9.45) * mm});
            skLineSegment(sketch, "E48.9.0.0", {"start": v(-5.09, 11.12) * mm, "end": v(-5.57, 9.46) * mm});
            skLineSegment(sketch, "E48.9.0.1", {"start": v(-5.09, 11.12) * mm, "end": v(-4.06, 11.12) * mm});
            skLineSegment(sketch, "E48.9.0.2", {"start": v(-5.57, 9.46) * mm, "end": v(-3.59, 9.45) * mm});
            skLineSegment(sketch, "E48.9.0.3", {"start": v(-4.06, 11.12) * mm, "end": v(-3.59, 9.45) * mm});
            skLineSegment(sketch, "E48.10.0.0", {"start": v(-2.4, 11.12) * mm, "end": v(-2.87, 9.46) * mm});
            skLineSegment(sketch, "E48.10.0.1", {"start": v(-2.4, 11.12) * mm, "end": v(-1.37, 11.12) * mm});
            skLineSegment(sketch, "E48.10.0.2", {"start": v(-2.87, 9.46) * mm, "end": v(-0.9, 9.45) * mm});
            skLineSegment(sketch, "E48.10.0.3", {"start": v(-1.37, 11.12) * mm, "end": v(-0.9, 9.45) * mm});
            skLineSegment(sketch, "E48.11.0.0", {"start": v(0.3, 11.12) * mm, "end": v(-0.18, 9.46) * mm});
            skLineSegment(sketch, "E48.11.0.1", {"start": v(0.3, 11.12) * mm, "end": v(1.33, 11.12) * mm});
            skLineSegment(sketch, "E48.11.0.2", {"start": v(-0.18, 9.46) * mm, "end": v(1.8, 9.45) * mm});
            skLineSegment(sketch, "E48.11.0.3", {"start": v(1.33, 11.12) * mm, "end": v(1.8, 9.45) * mm});
            skLineSegment(sketch, "E48.12.0.1", {"start": v(2.99, 11.12) * mm, "end": v(4.02, 11.12) * mm});
            skLineSegment(sketch, "E48.12.0.2", {"start": v(2.51, 9.46) * mm, "end": v(4.49, 9.45) * mm});
            skLineSegment(sketch, "E48.12.0.3", {"start": v(4.02, 11.12) * mm, "end": v(4.49, 9.45) * mm});
            skLineSegment(sketch, "E48.13.0.0", {"start": v(5.68, 11.12) * mm, "end": v(5.2, 9.46) * mm});
            skLineSegment(sketch, "E48.13.0.1", {"start": v(5.68, 11.12) * mm, "end": v(6.71, 11.12) * mm});
            skLineSegment(sketch, "E48.13.0.2", {"start": v(5.2, 9.46) * mm, "end": v(7.18, 9.45) * mm});
            skLineSegment(sketch, "E48.13.0.3", {"start": v(6.71, 11.12) * mm, "end": v(7.18, 9.45) * mm});
            skLineSegment(sketch, "E48.14.0.0", {"start": v(8.37, 11.12) * mm, "end": v(7.9, 9.46) * mm});
            skLineSegment(sketch, "E48.14.0.1", {"start": v(8.37, 11.12) * mm, "end": v(9.4, 11.12) * mm});
            skLineSegment(sketch, "E48.14.0.2", {"start": v(7.9, 9.46) * mm, "end": v(9.87, 9.45) * mm});
            skLineSegment(sketch, "E48.14.0.3", {"start": v(9.4, 11.12) * mm, "end": v(9.87, 9.45) * mm});
            skLineSegment(sketch, "E48.15.0.0", {"start": v(11.06, 11.12) * mm, "end": v(10.59, 9.46) * mm});
            skLineSegment(sketch, "E48.15.0.1", {"start": v(11.06, 11.12) * mm, "end": v(12.1, 11.12) * mm});
            skLineSegment(sketch, "E48.15.0.2", {"start": v(10.59, 9.46) * mm, "end": v(12.57, 9.45) * mm});
            skLineSegment(sketch, "E48.15.0.3", {"start": v(12.1, 11.12) * mm, "end": v(12.57, 9.45) * mm});
            skLineSegment(sketch, "E48.16.0.0", {"start": v(13.3, 11.98) * mm, "end": v(13.3, 9.46) * mm});
            skLineSegment(sketch, "E48.16.0.1", {"start": v(13.3, 11.98) * mm, "end": v(15.26, 11.98) * mm});
            skLineSegment(sketch, "E48.16.0.2", {"start": v(13.3, 9.46) * mm, "end": v(15.26, 9.45) * mm});
            skLineSegment(sketch, "E48.16.0.3", {"start": v(15.26, 11.98) * mm, "end": v(15.26, 9.45) * mm});
            skLineSegment(sketch, "E48.direction1", {"start": v(-29.8, 9.46) * mm, "end": v(-27.1, 9.46) * mm, "construction": true});
            skLineSegment(sketch, "E49", {"start": v(2.99, 11.12) * mm, "end": v(2.51, 9.46) * mm});
            skLineSegment(sketch, "E50.bottom", {"start": v(15.24, 9.46) * mm, "end": v(-29.8, 9.46) * mm});
            skLineSegment(sketch, "E50.top", {"start": v(15.24, 8.2) * mm, "end": v(-29.8, 8.2) * mm});
            skLineSegment(sketch, "E50.left", {"start": v(15.24, 9.46) * mm, "end": v(15.24, 8.2) * mm});
            skLineSegment(sketch, "E50.right", {"start": v(-29.8, 9.46) * mm, "end": v(-29.8, 8.2) * mm});
            skSolve(sketch);
        }
        {
            var Q0;
            Q0=makeQuery(id+"F40.imprint","IMPRINT",FACE,{"disambiguationData":[TD([[makeQuery(id+"F40.imprint","IMPRINT",EDGE,{"derivedFrom":sQuery(id+"F40.wireOp",EDGE,"kKsKmWk8-I0HW-xY3J-H7Ep-pKHz2QezjDSn")}),1.0]])]});
            var Q1;
            Q1 = qSketchRegion(id + "F40", true);
            extrude(context, id + "F41", {"entities" : qUnion([Q0, Q1]), "oppositeDirection" : true, "depth" : 8.43 * mm, "offsetDistance" : 25.4 * mm});
        }
        {
            var Q0;
            {var subQ0=makeQuery(id+"F30.opExtrude","CAP_FACE",FACE,{"disambiguationData":[OSD([sQuery(id+"F29.wireOp",EDGE,"E23"),sQuery(id+"F29.wireOp",EDGE,"E33"),sQuery(id+"F29.wireOp",EDGE,"E34"),sQuery(id+"F29.wireOp",EDGE,"E35.MirrorCS"),sQuery(id+"F29.wireOp",EDGE,"E36.MirrorCS"),sQuery(id+"F29.wireOp",EDGE,"E37")])],"isStart":false});Q0=makeQuery(id+"F32.opBoolean","MERGE",FACE,{"derivedFrom":[subQ0,makeQuery(id+"F31.opPattern","COPY",FACE,{"derivedFrom":subQ0,"instanceName":"1"}),makeQuery(id+"F31.opPattern","COPY",FACE,{"derivedFrom":subQ0,"instanceName":"2"}),makeQuery(id+"F31.opPattern","COPY",FACE,{"derivedFrom":subQ0,"instanceName":"3"}),makeQuery(id+"F31.opPattern","COPY",FACE,{"derivedFrom":subQ0,"instanceName":"4"}),makeQuery(id+"F31.opPattern","COPY",FACE,{"derivedFrom":subQ0,"instanceName":"5"}),makeQuery(id+"F31.opPattern","COPY",FACE,{"derivedFrom":subQ0,"instanceName":"6"}),makeQuery(id+"F31.opPattern","COPY",FACE,{"derivedFrom":subQ0,"instanceName":"7"})]});}
            var sketch = newSketch(context, id + "F42", { "sketchPlane" : qUnion([Q0])});
            skCircle(sketch, "E51", {"center": v(42.36, 55.53) * mm, "radius": 3.18 * mm});
            skCircle(sketch, "E52", {"center": v(42.36, 55.53) * mm, "radius": 4.7 * mm, "construction": true});
            skCircle(sketch, "E53", {"center": v(42.36, 55.53) * mm, "radius": 4.06 * mm, "construction": true});
            skLineSegment(sketch, "E54", {"start": v(42.36, 55.53) * mm, "end": v(42.36, 61.22) * mm, "construction": true});
            skLineSegment(sketch, "E55", {"start": v(42.36, 55.53) * mm, "end": v(41.82, 61.33) * mm, "construction": true});
            skLineSegment(sketch, "E56", {"start": v(41.99, 59.58) * mm, "end": v(45.99, 59.95) * mm, "construction": true});
            skLineSegment(sketch, "E57", {"start": v(41.99, 59.58) * mm, "end": v(45.94, 58.54) * mm, "construction": true});
            skCircle(sketch, "E58", {"center": v(42.36, 55.53) * mm, "radius": 3.82 * mm, "construction": true});
            skCircle(sketch, "E59", {"center": v(41.99, 59.58) * mm, "radius": 1.44 * mm, "construction": true});
            skCircle(sketch, "E60", {"center": v(43.37, 59.21) * mm, "radius": 1.44 * mm, "construction": true});
            skArc(sketch, "E61", {"start": v(42.36, 60.23) * mm, "mid": v(42.12, 59.93) * mm, "end": v(41.99, 59.58) * mm});
            skArc(sketch, "E62", {"start": v(41.99, 59.58) * mm, "mid": v(41.94, 59.13) * mm, "end": v(42.04, 58.7) * mm});
            skArc(sketch, "E63.MirrorCS", {"start": v(42.36, 60.23) * mm, "mid": v(42.6, 59.93) * mm, "end": v(42.74, 59.58) * mm});
            skArc(sketch, "E64.MirrorCS", {"start": v(42.74, 59.58) * mm, "mid": v(42.78, 59.13) * mm, "end": v(42.68, 58.7) * mm});
            skCircle(sketch, "E65", {"center": v(42.36, 55.53) * mm, "radius": 0.89 * mm});
            skSolve(sketch);
        }
        {
            var Q0;
            Q0=makeQuery(id+"F42.imprint","IMPRINT",FACE,{"disambiguationData":[TD([[makeQuery(id+"F42.imprint","IMPRINT",EDGE,{"derivedFrom":sQuery(id+"F42.wireOp",EDGE,"lJrdpfBb-uI2E-rS3P-qHU8-fVFrq39TFAc0")}),1.0]])]});
            var Q1;
            {var subQ0=sQuery(id+"F42.wireOp",EDGE,"E51");var subQ1=makeQuery(id+"F42.imprint","INTERSECT",VERTEX,{"derivedFrom":[subQ0,sQuery(id+"F42.wireOp",EDGE,"2Iw7Z1zx-kL9v-oPZk-BEM1-MFSy77lXLglC")]});Q1=makeQuery(id+"F42.imprint","IMPRINT",FACE,{"disambiguationData":[TD([[makeQuery(id+"F42.imprint","IMPRINT",EDGE,{"disambiguationData":[TD([[subQ1,1.0]])],"derivedFrom":subQ0}),1.0]])]});}
            var Q2;
            {var subQ1=sQuery(id+"F42.wireOp",EDGE,"COxInbig-2hFa-vJEt-9ibK-O6dTQdwu1tOu");Q2=makeQuery(id+"F42.imprint","IMPRINT",FACE,{"disambiguationData":[TD([[makeQuery(id+"F42.imprint","IMPRINT",EDGE,{"derivedFrom":subQ1}),1.0]])]});}
            var Q3;
            Q3=makeQuery(id+"F42.imprint","IMPRINT",FACE,{"disambiguationData":[TD([[makeQuery(id+"F42.imprint","IMPRINT",EDGE,{"derivedFrom":sQuery(id+"F42.wireOp",EDGE,"E61")}),1.0]])]});
            extrude(context, id + "F43", {"entities" : qUnion([Q0, Q1, Q2, Q3]), "depth" : 5.7 * mm, "offsetDistance" : 25.4 * mm});
        }
        {
            var Q0;
            Q0=makeQuery(id+"F43.opExtrude","SWEPT_BODY",BODY,{"disambiguationData":[OSD([sQuery(id+"F42.wireOp",EDGE,"E51"),sQuery(id+"F42.wireOp",EDGE,"lJrdpfBb-uI2E-rS3P-qHU8-fVFrq39TFAc0"),sQuery(id+"F42.wireOp",EDGE,"2Iw7Z1zx-kL9v-oPZk-BEM1-MFSy77lXLglC"),sQuery(id+"F42.wireOp",EDGE,"da0e9be2-ffc6-4457-b6fb-16e6c54a573a0.MirrorCS"),sQuery(id+"F42.wireOp",EDGE,"b36d090a-fde8-4ae0-8fd2-8ef5cf2a751c0.MirrorCS"),sQuery(id+"F42.wireOp",EDGE,"8LBACDPT-uP2y-6KeS-UC7q-9f6mYUzfWrku")])]});
            var Q1;
            Q1=makeQuery(id+"F43.opExtrude","SWEPT_FACE",FACE,{"disambiguationData":[OSD([sQuery(id+"F42.wireOp",EDGE,"E51")])]});
            circularPattern(context, id + "F44", {"entities" : qUnion([Q0]), "axis" : qUnion([Q1]), "angle" : 360 * degree, "instanceCount" : 16, "equalSpace" : true});
        }
    });
